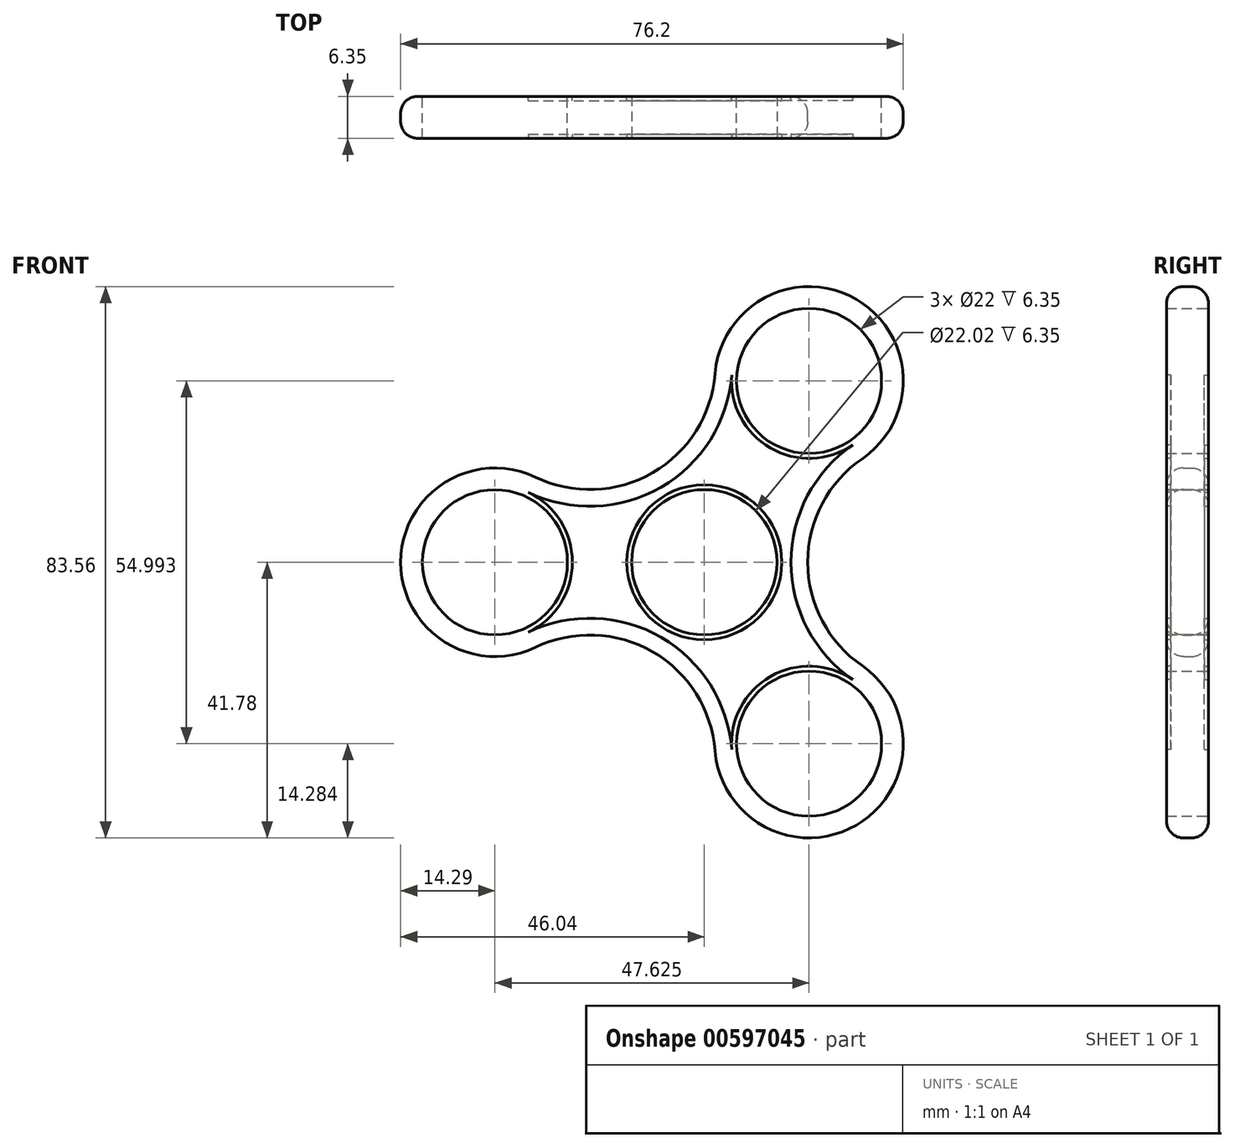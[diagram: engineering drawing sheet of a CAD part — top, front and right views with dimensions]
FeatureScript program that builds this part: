
annotation { "Feature Type Name" : "Feature", "Feature Type Description" : "" }
export const myFeature = defineFeature(function(context is Context, id is Id, definition is map)
    precondition{}
    {
        {
            var Q0;
            Q0=qCreatedBy(makeId("Front.planeOp"),FACE);
            var sketch = newSketch(context, id + "F0", { "sketchPlane" : qUnion([Q0])});
            skArc(sketch, "E0", {"start": v(23.95, 15.71) * mm, "mid": v(15.68, 0) * mm, "end": v(23.95, -15.71) * mm});
            skArc(sketch, "E1", {"start": v(1.63, -28.6) * mm, "mid": v(-7.84, -13.58) * mm, "end": v(-25.58, -12.89) * mm});
            skArc(sketch, "E2", {"start": v(-25.58, 12.89) * mm, "mid": v(-7.84, 13.58) * mm, "end": v(1.63, 28.6) * mm});
            skArc(sketch, "E3.0", {"start": v(23.95, 15.71) * mm, "mid": v(23.02, 39.87) * mm, "end": v(1.63, 28.6) * mm});
            skCircle(sketch, "E4.0", {"center": v(15.88, 27.5) * mm, "radius": 11 * mm});
            skCircle(sketch, "E5.0", {"center": v(0, 0) * mm, "radius": 14.29 * mm});
            skCircle(sketch, "E6.0", {"center": v(0, 0) * mm, "radius": 11 * mm});
            skArc(sketch, "E7.0", {"start": v(1.63, -28.6) * mm, "mid": v(23.02, -39.87) * mm, "end": v(23.95, -15.71) * mm});
            skCircle(sketch, "E8.0", {"center": v(15.87, -27.5) * mm, "radius": 11 * mm});
            skArc(sketch, "E9.0", {"start": v(-25.58, 12.89) * mm, "mid": v(-46.04, 0) * mm, "end": v(-25.58, -12.89) * mm});
            skCircle(sketch, "E10.0", {"center": v(-31.75, 0) * mm, "radius": 11 * mm});
            skSolve(sketch);
        }
        {
            var Q0;
            Q0=makeQuery(id+"F3jBpgvP5Y4heRG_0.imprint","IMPRINT",FACE,{"disambiguationData":[TD([[makeQuery(id+"F3jBpgvP5Y4heRG_0.imprint","IMPRINT",EDGE,{"derivedFrom":sQuery(id+"F3jBpgvP5Y4heRG_0.wireOp",EDGE,"0sE3iGKY-7zmb-4Tw1-qnUl-LUcS0hapwhKu")}),1.0]])]});
            var Q1;
            Q1=makeQuery(id+"F3jBpgvP5Y4heRG_0.imprint","IMPRINT",FACE,{"disambiguationData":[TD([[makeQuery(id+"F3jBpgvP5Y4heRG_0.imprint","IMPRINT",EDGE,{"derivedFrom":sQuery(id+"F3jBpgvP5Y4heRG_0.wireOp",EDGE,"1715efbe-12b4-44a4-8e44-3d016f07ad60.2.0")}),-1.0]])]});
            var Q2;
            Q2=makeQuery(id+"F3jBpgvP5Y4heRG_0.imprint","IMPRINT",FACE,{"disambiguationData":[TD([[makeQuery(id+"F3jBpgvP5Y4heRG_0.imprint","IMPRINT",EDGE,{"derivedFrom":sQuery(id+"F3jBpgvP5Y4heRG_0.wireOp",EDGE,"1715efbe-12b4-44a4-8e44-3d016f07ad60.1.0")}),-1.0]])]});
            var Q3;
            Q3=makeQuery(id+"F3jBpgvP5Y4heRG_0.imprint","IMPRINT",FACE,{"disambiguationData":[TD([[makeQuery(id+"F3jBpgvP5Y4heRG_0.imprint","IMPRINT",EDGE,{"derivedFrom":sQuery(id+"F3jBpgvP5Y4heRG_0.wireOp",EDGE,"1715efbe-12b4-44a4-8e44-3d016f07ad60.2.2")}),-1.0]])]});
            var Q4;
            {var subQ1=sQuery(id+"F0.wireOp",EDGE,"E0");Q4=makeQuery(id+"F0.imprint","IMPRINT",FACE,{"disambiguationData":[TD([[makeQuery(id+"F0.imprint","IMPRINT",EDGE,{"derivedFrom":subQ1}),-1.0]])]});}
            extrude(context, id + "F1", {"entities" : qUnion([Q0, Q1, Q2, Q3, Q4]), "depth" : 6.35 * mm, "offsetDistance" : 25.4 * mm});
        }
        {
            var Q0;
            Q0=makeQuery(id+"F1.opExtrude","CAP_FACE",FACE,{"disambiguationData":[OSD([sQuery(id+"F0.wireOp",EDGE,"E0"),sQuery(id+"F0.wireOp",EDGE,"E1"),sQuery(id+"F0.wireOp",EDGE,"E2"),sQuery(id+"F0.wireOp",EDGE,"E3.0"),sQuery(id+"F0.wireOp",EDGE,"E4.0"),sQuery(id+"F0.wireOp",EDGE,"E5.0"),sQuery(id+"F0.wireOp",EDGE,"E7.0"),sQuery(id+"F0.wireOp",EDGE,"E8.0"),sQuery(id+"F0.wireOp",EDGE,"E9.0"),sQuery(id+"F0.wireOp",EDGE,"E10.0")])],"isStart":false});
            var sketch = newSketch(context, id + "F2", { "sketchPlane" : qUnion([Q0])});
            skCircle(sketch, "E11.0", {"center": v(0, 0) * mm, "radius": 14.29 * mm});
            skCircle(sketch, "E12", {"center": v(0, 0) * mm, "radius": 11.01 * mm});
            skSolve(sketch);
        }
        {
            var Q0;
            Q0 = qSketchRegion(id + "F2", true);
            extrude(context, id + "F3", {"entities" : qUnion([Q0]), "operationType" : NewBodyOperationType.ADD, "oppositeDirection" : true, "depth" : 6.35 * mm, "offsetDistance" : 25.4 * mm});
        }
        {
            var Q0;
            Q0=makeQuery(id+"F1.opExtrude","CAP_EDGE",EDGE,{"disambiguationData":[OSD([sQuery(id+"F0.wireOp",EDGE,"E2")])],"isStart":false});
            var Q1;
            Q1=makeQuery(id+"F1.opExtrude","CAP_EDGE",EDGE,{"disambiguationData":[OSD([sQuery(id+"F0.wireOp",EDGE,"E0")])],"isStart":true});
            fillet(context, id + "F4", {"entities" : qUnion([Q0, Q1]), "radius" : 2.54 * mm, "tangentPropagation" : true, "allowEdgeOverflow" : false});
        }
        {
            var Q0;
            Q0=makeQuery(id+"F3.boolean.opBoolean","MERGE",FACE,{"derivedFrom":[makeQuery(id+"F1.opExtrude","CAP_FACE",FACE,{"disambiguationData":[OSD([sQuery(id+"F0.wireOp",EDGE,"E0"),sQuery(id+"F0.wireOp",EDGE,"E1"),sQuery(id+"F0.wireOp",EDGE,"E2"),sQuery(id+"F0.wireOp",EDGE,"E3.0"),sQuery(id+"F0.wireOp",EDGE,"E4.0"),sQuery(id+"F0.wireOp",EDGE,"E5.0"),sQuery(id+"F0.wireOp",EDGE,"E7.0"),sQuery(id+"F0.wireOp",EDGE,"E8.0"),sQuery(id+"F0.wireOp",EDGE,"E9.0"),sQuery(id+"F0.wireOp",EDGE,"E10.0")])],"isStart":false}),makeQuery(id+"F3.opExtrude","CAP_FACE",FACE,{"disambiguationData":[OSD([sQuery(id+"F2.wireOp",EDGE,"E11.0"),sQuery(id+"F2.wireOp",EDGE,"E12")])],"isStart":true})]});
            var sketch = newSketch(context, id + "F5", { "sketchPlane" : qUnion([Q0])});
            skArc(sketch, "E13.0.0", {"start": v(-26.68, -10.6) * mm, "mid": v(-6.57, -11.38) * mm, "end": v(4.16, -28.4) * mm});
            skArc(sketch, "E13.0.1", {"start": v(4.16, -28.4) * mm, "mid": v(21.75, -37.67) * mm, "end": v(22.52, -17.8) * mm});
            skArc(sketch, "E13.0.2", {"start": v(22.52, -17.8) * mm, "mid": v(13.14, 0) * mm, "end": v(22.52, 17.8) * mm});
            skArc(sketch, "E13.0.3", {"start": v(22.52, 17.8) * mm, "mid": v(21.75, 37.67) * mm, "end": v(4.16, 28.4) * mm});
            skArc(sketch, "E13.0.4", {"start": v(4.16, 28.4) * mm, "mid": v(-6.57, 11.38) * mm, "end": v(-26.68, 10.6) * mm});
            skArc(sketch, "E13.0.5", {"start": v(-26.68, 10.6) * mm, "mid": v(-43.5, 0) * mm, "end": v(-26.68, -10.6) * mm});
            skCircle(sketch, "E14", {"center": v(15.88, 27.5) * mm, "radius": 11.75 * mm});
            skCircle(sketch, "E15", {"center": v(-31.75, 0) * mm, "radius": 11.75 * mm});
            skCircle(sketch, "E16", {"center": v(15.87, -27.5) * mm, "radius": 11.75 * mm});
            skCircle(sketch, "E17", {"center": v(0, 0) * mm, "radius": 11.75 * mm});
            skSolve(sketch);
        }
        {
            var Q0;
            {var subQ3=sQuery(id+"F5.wireOp",EDGE,"E13.0.0");Q0=makeQuery(id+"F5.imprint","IMPRINT",FACE,{"disambiguationData":[TD([[makeQuery(id+"F5.imprint","IMPRINT",EDGE,{"derivedFrom":subQ3}),1.0]])]});}
            extrude(context, id + "F6", {"entities" : qUnion([Q0]), "operationType" : NewBodyOperationType.REMOVE, "oppositeDirection" : true, "depth" : 0.64 * mm, "offsetDistance" : 25.4 * mm});
        }
        {
            var Q0;
            Q0=makeQuery(id+"F3.boolean.opBoolean","MERGE",FACE,{"derivedFrom":[makeQuery(id+"F1.opExtrude","CAP_FACE",FACE,{"disambiguationData":[OSD([sQuery(id+"F0.wireOp",EDGE,"E0"),sQuery(id+"F0.wireOp",EDGE,"E1"),sQuery(id+"F0.wireOp",EDGE,"E2"),sQuery(id+"F0.wireOp",EDGE,"E3.0"),sQuery(id+"F0.wireOp",EDGE,"E4.0"),sQuery(id+"F0.wireOp",EDGE,"E5.0"),sQuery(id+"F0.wireOp",EDGE,"E7.0"),sQuery(id+"F0.wireOp",EDGE,"E8.0"),sQuery(id+"F0.wireOp",EDGE,"E9.0"),sQuery(id+"F0.wireOp",EDGE,"E10.0")])],"isStart":true}),makeQuery(id+"F3.opExtrude","CAP_FACE",FACE,{"disambiguationData":[OSD([sQuery(id+"F2.wireOp",EDGE,"E11.0"),sQuery(id+"F2.wireOp",EDGE,"E12")])],"isStart":false})]});
            var sketch = newSketch(context, id + "F7", { "sketchPlane" : qUnion([Q0])});
            skArc(sketch, "E18.0.0", {"start": v(-4.16, -28.4) * mm, "mid": v(6.57, -11.38) * mm, "end": v(26.68, -10.6) * mm});
            skArc(sketch, "E18.0.1", {"start": v(26.68, -10.6) * mm, "mid": v(43.5, 0) * mm, "end": v(26.68, 10.6) * mm});
            skArc(sketch, "E18.0.2", {"start": v(26.68, 10.6) * mm, "mid": v(6.57, 11.38) * mm, "end": v(-4.16, 28.4) * mm});
            skArc(sketch, "E18.0.3", {"start": v(-4.16, 28.4) * mm, "mid": v(-21.75, 37.67) * mm, "end": v(-22.52, 17.8) * mm});
            skArc(sketch, "E18.0.4", {"start": v(-22.52, 17.8) * mm, "mid": v(-13.14, 0) * mm, "end": v(-22.52, -17.8) * mm});
            skArc(sketch, "E18.0.5", {"start": v(-22.52, -17.8) * mm, "mid": v(-21.75, -37.67) * mm, "end": v(-4.16, -28.4) * mm});
            skCircle(sketch, "E19", {"center": v(31.75, 0) * mm, "radius": 11.75 * mm});
            skCircle(sketch, "E20", {"center": v(-15.87, -27.5) * mm, "radius": 11.75 * mm});
            skCircle(sketch, "E21", {"center": v(-15.88, 27.5) * mm, "radius": 11.75 * mm});
            skCircle(sketch, "E22", {"center": v(0, 0) * mm, "radius": 11.75 * mm});
            skSolve(sketch);
        }
        {
            var Q0;
            {var subQ1=sQuery(id+"F7.wireOp",EDGE,"E18.0.0");Q0=makeQuery(id+"F7.imprint","IMPRINT",FACE,{"disambiguationData":[TD([[makeQuery(id+"F7.imprint","IMPRINT",EDGE,{"derivedFrom":subQ1}),1.0]])]});}
            extrude(context, id + "F8", {"entities" : qUnion([Q0]), "operationType" : NewBodyOperationType.REMOVE, "oppositeDirection" : true, "depth" : 0.64 * mm, "offsetDistance" : 25.4 * mm});
        }
    });
